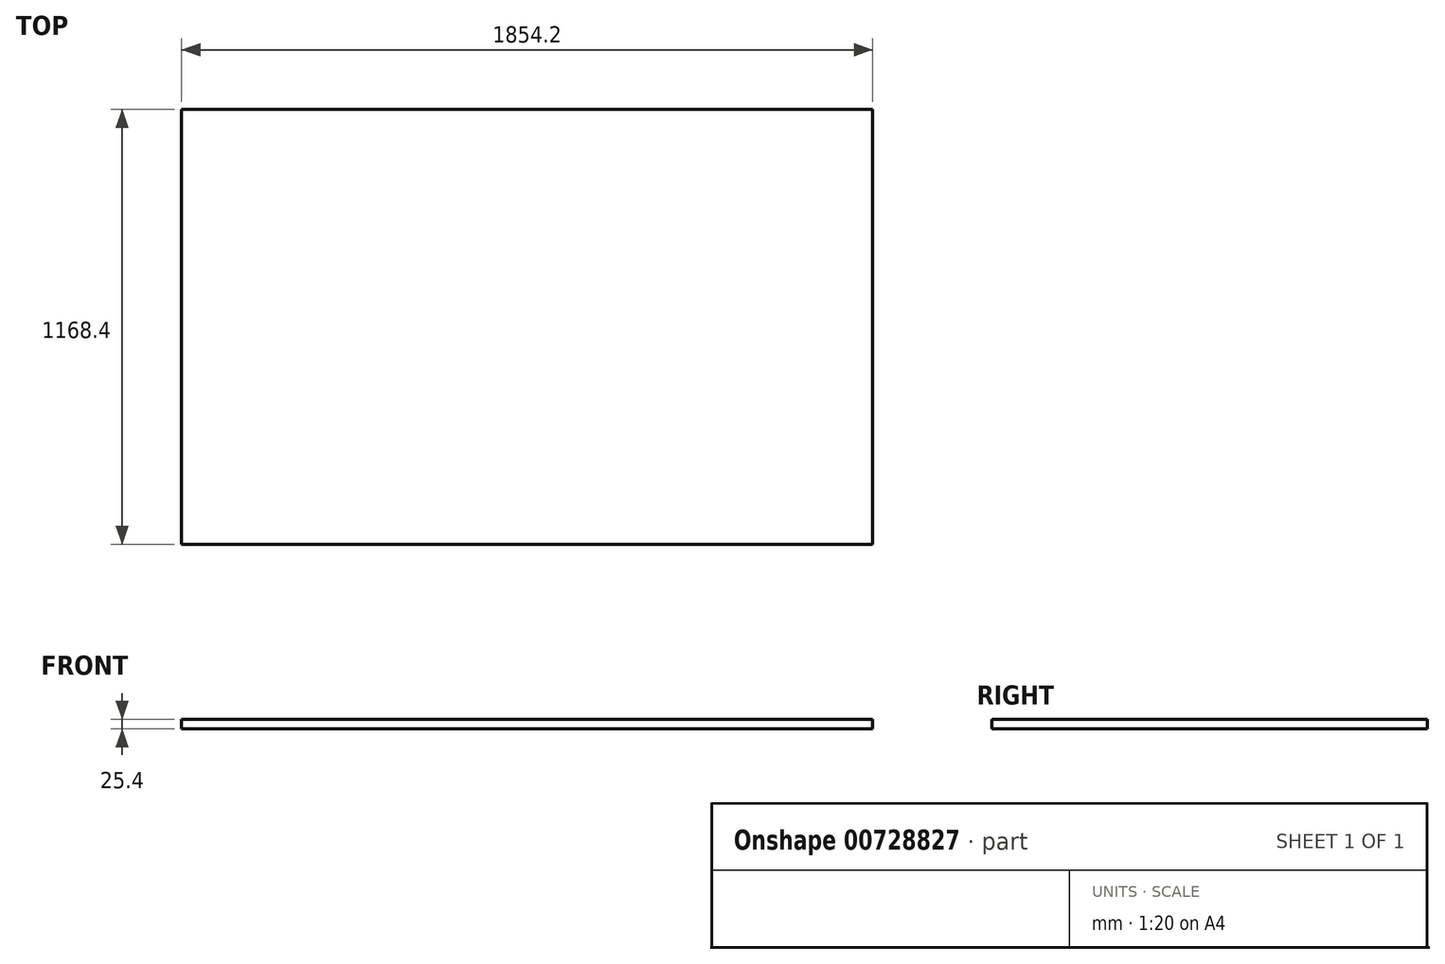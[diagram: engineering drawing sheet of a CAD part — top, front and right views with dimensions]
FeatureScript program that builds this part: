
annotation { "Feature Type Name" : "Feature", "Feature Type Description" : "" }
export const myFeature = defineFeature(function(context is Context, id is Id, definition is map)
    precondition{}
    {
        {
            var Q0;
            Q0=qCreatedBy(makeId("Top.planeOp"),FACE);
            var sketch = newSketch(context, id + "F0", { "sketchPlane" : qUnion([Q0])});
            skLineSegment(sketch, "E0.bottom", {"start": v(-910.5, 612.44) * mm, "end": v(943.7, 612.44) * mm});
            skLineSegment(sketch, "E0.top", {"start": v(-910.5, -555.96) * mm, "end": v(943.7, -555.96) * mm});
            skLineSegment(sketch, "E0.left", {"start": v(-910.5, 612.44) * mm, "end": v(-910.5, -555.96) * mm});
            skLineSegment(sketch, "E0.right", {"start": v(943.7, 612.44) * mm, "end": v(943.7, -555.96) * mm});
            skSolve(sketch);
        }
        {
            var Q0;
            Q0=makeQuery(id+"F0.imprint","IMPRINT",FACE,{"disambiguationData":[TD([[makeQuery(id+"F0.imprint","IMPRINT",EDGE,{"derivedFrom":sQuery(id+"F0.wireOp",EDGE,"E0.bottom")}),-1.0]])]});
            extrude(context, id + "F1", {"entities" : qUnion([Q0]), "depth" : 25.4 * mm, "offsetDistance" : 25.4 * mm});
        }
    });
